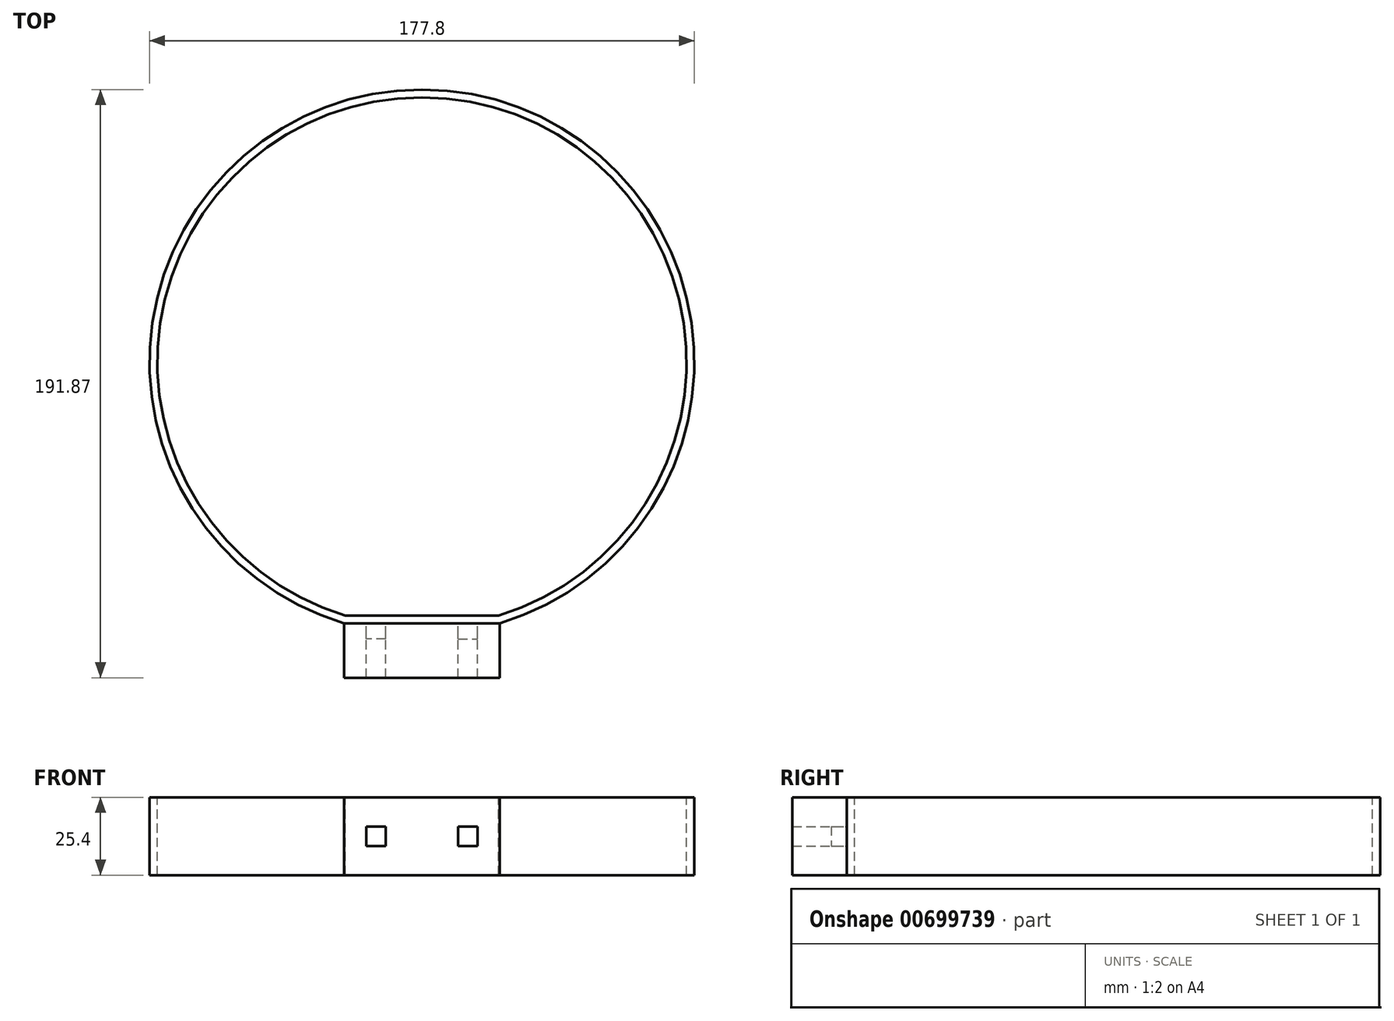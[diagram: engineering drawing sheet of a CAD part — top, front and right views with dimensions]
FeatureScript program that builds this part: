
annotation { "Feature Type Name" : "Feature", "Feature Type Description" : "" }
export const myFeature = defineFeature(function(context is Context, id is Id, definition is map)
    precondition{}
    {
        {
            var Q0;
            Q0=qCreatedBy(makeId("Front.planeOp"),FACE);
            var sketch = newSketch(context, id + "F0", { "sketchPlane" : qUnion([Q0])});
            skLineSegment(sketch, "E0.0.0", {"start": v(-18.24, -4.82) * mm, "end": v(-18.24, -4.82) * mm});
            skLineSegment(sketch, "E0.0.1", {"start": v(-25.4, -10.25) * mm, "end": v(-25.4, -12.7) * mm});
            skLineSegment(sketch, "E0.0.2", {"start": v(-25.4, -12.7) * mm, "end": v(-25.4, -10.25) * mm});
            skLineSegment(sketch, "E0.0.3", {"start": v(-18.24, -4.82) * mm, "end": v(-18.24, -4.82) * mm});
            skLineSegment(sketch, "E1", {"start": v(-18.17, -3.17) * mm, "end": v(-18.17, 3.17) * mm});
            skLineSegment(sketch, "E2", {"start": v(-18.17, 3.18) * mm, "end": v(-11.82, 3.18) * mm});
            skLineSegment(sketch, "E3", {"start": v(-11.82, 3.17) * mm, "end": v(-11.82, -3.17) * mm});
            skLineSegment(sketch, "E4", {"start": v(-11.82, -3.17) * mm, "end": v(-18.17, -3.17) * mm});
            skLineSegment(sketch, "E5", {"start": v(11.82, -3.17) * mm, "end": v(18.17, -3.17) * mm});
            skLineSegment(sketch, "E6", {"start": v(18.17, -3.17) * mm, "end": v(18.17, 3.17) * mm});
            skLineSegment(sketch, "E7", {"start": v(18.17, 3.17) * mm, "end": v(11.82, 3.17) * mm});
            skLineSegment(sketch, "E8", {"start": v(11.82, 3.17) * mm, "end": v(11.82, -3.17) * mm});
            skLineSegment(sketch, "E9.0", {"start": v(-25.4, 12.7) * mm, "end": v(-25.4, -12.7) * mm});
            skLineSegment(sketch, "E10.0.2", {"start": v(-25.4, -12.7) * mm, "end": v(-25.4, 12.7) * mm});
            skLineSegment(sketch, "E11.0", {"start": v(-25.4, 12.7) * mm, "end": v(25.4, 12.7) * mm});
            skLineSegment(sketch, "E12.0.0", {"start": v(-25.4, -12.7) * mm, "end": v(25.4, -12.7) * mm});
            skLineSegment(sketch, "E12.0.1", {"start": v(25.4, 12.7) * mm, "end": v(25.4, -12.7) * mm});
            skLineSegment(sketch, "E12.0.2", {"start": v(25.4, 12.7) * mm, "end": v(-25.4, 12.7) * mm});
            skLineSegment(sketch, "E13", {"start": v(0, -12.7) * mm, "end": v(0, 12.7) * mm, "construction": true});
            skLineSegment(sketch, "E14", {"start": v(0, 0) * mm, "end": v(5.7, 0) * mm, "construction": true});
            skPoint(sketch, "E15", {"position": v(11.82, 0) * mm});
            skPoint(sketch, "E16.0", {"position": v(0, 0) * mm});
            skSolve(sketch);
        }
        {
            var Q0;
            Q0=makeQuery(id+"F0.imprint","IMPRINT",FACE,{"disambiguationData":[TD([[makeQuery(id+"F0.imprint","IMPRINT",EDGE,{"derivedFrom":sQuery(id+"F0.wireOp",EDGE,"E1")}),-1.0]])]});
            var Q1;
            Q1=makeQuery(id+"F0.imprint","IMPRINT",FACE,{"disambiguationData":[TD([[makeQuery(id+"F0.imprint","IMPRINT",EDGE,{"derivedFrom":sQuery(id+"F0.wireOp",EDGE,"E5")}),1.0]])]});
            extrude(context, id + "F1", {"entities" : qUnion([Q0, Q1]), "depth" : 5.08 * mm, "offsetDistance" : 25.4 * mm});
        }
        {
            var Q0;
            Q0 = qSketchRegion(id + "F0", true);
            extrude(context, id + "F2", {"entities" : qUnion([Q0]), "depth" : 17.78 * mm, "offsetDistance" : 25.4 * mm});
        }
        {
            var Q0;
            Q0=qCreatedBy(makeId("Top.planeOp"),FACE);
            var sketch = newSketch(context, id + "F3", { "sketchPlane" : qUnion([Q0])});
            skLineSegment(sketch, "E17.0.0", {"start": v(25.4, 0) * mm, "end": v(-25.4, 0) * mm});
            skLineSegment(sketch, "E17.0.1", {"start": v(-25.4, 0) * mm, "end": v(-25.4, -17.78) * mm});
            skLineSegment(sketch, "E17.0.2", {"start": v(-25.4, -17.78) * mm, "end": v(25.4, -17.78) * mm});
            skLineSegment(sketch, "E17.0.3", {"start": v(25.4, -17.78) * mm, "end": v(25.4, 0) * mm});
            skPoint(sketch, "E18.0", {"position": v(0, 0) * mm});
            skArc(sketch, "E19", {"start": v(25.4, 0) * mm, "mid": v(0, 174.1) * mm, "end": v(-25.4, 0) * mm});
            skPoint(sketch, "E19.third.point", {"position": v(83.82, 114.8) * mm});
            skSolve(sketch);
        }
        {
            var Q0;
            Q0=makeQuery(id+"F3.imprint","IMPRINT",FACE,{"disambiguationData":[TD([[makeQuery(id+"F3.imprint","IMPRINT",EDGE,{"derivedFrom":sQuery(id+"F3.wireOp",EDGE,"E17.0.0")}),-1.0]])]});
            cPlane(context, id + "F4", {"entities" : qUnion([Q0]), "cplaneType" : CPlaneType.OFFSET, "offset" : 12.7 * mm, "width" : 152.4 * mm, "height" : 152.4 * mm});
        }
        {
            var Q0;
            Q0=qCreatedBy(id+"F4.planeOp",FACE);
            var sketch = newSketch(context, id + "F5", { "sketchPlane" : qUnion([Q0])});
            skLineSegment(sketch, "E20.0.0", {"start": v(-25.4, 0) * mm, "end": v(25.4, 0) * mm});
            skArc(sketch, "E20.0.1", {"start": v(25.4, 0) * mm, "mid": v(0, 174.1) * mm, "end": v(-25.4, 0) * mm});
            skSolve(sketch);
        }
        {
            var Q0;
            Q0 = qSketchRegion(id + "F5", true);
            extrude(context, id + "F6", {"entities" : qUnion([Q0]), "oppositeDirection" : true, "depth" : 25.4 * mm, "offsetDistance" : 25.4 * mm});
        }
        {
            var Q0;
            Q0=makeQuery(id+"F6.opExtrude","CAP_FACE",FACE,{"disambiguationData":[OSD([sQuery(id+"F5.wireOp",EDGE,"E20.0.0"),sQuery(id+"F5.wireOp",EDGE,"E20.0.1")])],"isStart":true});
            var Q1;
            Q1=makeQuery(id+"F6.opExtrude","CAP_FACE",FACE,{"disambiguationData":[OSD([sQuery(id+"F5.wireOp",EDGE,"E20.0.0"),sQuery(id+"F5.wireOp",EDGE,"E20.0.1")])],"isStart":false});
            shell(context, id + "F7", {"entities" : qUnion([Q0, Q1]), "thickness" : 2.54 * mm});
        }
    });
